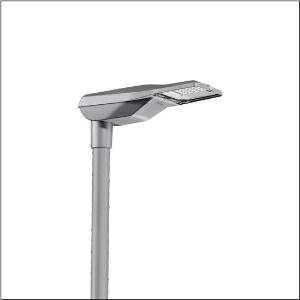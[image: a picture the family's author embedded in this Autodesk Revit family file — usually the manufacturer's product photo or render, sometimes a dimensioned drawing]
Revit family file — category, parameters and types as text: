
# Revit family: streetlight_sl_21_iq_micro___st1_0ab_5xe1m31d08db_7599
name_source: partatom
category: Lighting Fixtures
units: mm (PartAtom-declared; Revit-internal decimal feet)

## family parameters
Cut with Voids When Loaded = No
Host = Face
Light Source = No
Part Type = Normal
Room Calculation Point = No
Round Connector Dimension = Use Diameter
Shared = No

## types (1)
- --- (1 x LED, 4240 lm, 36.4 W, 3000K)
    Apparent Load = 36 VA
    CIE Flux Codes = 38 73 97 100 100
    Color Rendering = 70
    Color Temperature = 3000K
    Default Elevation = 1800 mm
    Description = Streetlight SL 21 iQ micro, mast luminaire, primary light control with lens, of PMMA, primary optical cover: cover, of toughened safety glass, transparent, light distribution: ST1.0aB, light emission: direct distribution, primary light characteristic: asymmetric, installation type: post-top, side-entry, LED, High Power LED, rated luminous flux: 4.240lm, luminous efficacy: 117lm/W, light colour: 730, colour temperature: 3000K, control: Auto-Match, Temp-Guard, Lumen-Switch, Night-Set, Smart-Wire, Light-Fading, Desk-Remote (wireless, voltage-free reading and setting of iQ features in the workshop via application-optimized NFC function/RFID function), optimised constant luminous flux control (CLO 2.0), presetting dimming linear, mains connection: 220..240V, AC, 50/60Hz, start of lifetime: 36W, end of service life: 38W, reduction: 16W, luminaire housing, of diecast aluminium, powder-coated, Siteco® metallic grey (DB 702S), corrosivity category C5 mid according to DIN EN ISO 12944, please order mast flange separately, inclination adjustable: 0°, 5°, 10°, 15°, sealing non-destructively replaceable, multi-level sealing system, length: 528mm, width: 235mm, height: 110mm, mast flange for spigot size: 42mm (side-entry): 5XC10008XM4, 60/48mm (side-entry/post-top): 5XC10108XM2, 76/60mm (side-entry/post-top): 5XC10108XM1, protection rating (complete): IP66, insulation class (complete): insulation class II (safety insulation), certification: CE, ENEC, ENEC+, VDE, impact resistance: IK09, permissible operating ambient temperature for outdoor applications: -40..+50°C, standard-compliant lighting for roads and squares, packaging unit: 1 piece

Light Distribution: ST1.0aB
    Height = 110 mm
    Lamp = 1 x LED
    Lamp Light Flux = 4240 lm
    Lamp Power = 36.4 W
    Lamp count = 1
    Length = 528 mm
    Luminous efficacy = 116 lm/W
    Manufacturer = Siteco
    ModVariant = No
    Model = 5XE1M31D08DB
    Number of Poles = 1
    OnlyDefault = Yes
    Power Factor = 1
    Product Name = Streetlight SL 21 iQ micro | ST1.0aB
    Product group = mast luminaire | pylon top
    ProductGroupID = 6100
    Protection Class = Protection class II
    Protection Degree = IP 66
    RLX_Detail_Level = 1
    RLX_Emergency_Light_Flux = 0 lm
    RLX_Emergency_Type = 0
    RLX_Emergency_Type_DB = No
    RlxData = <blob elided: 98913 chars, md5=5ed4cde0>
    Socket = socket
    Standby Power = 0 W
    System Light Flux = 4240 lm
    System Power = 36 W
    Type Comments = factory setting: luminous flux: 100 % | dim-lin: 254 | 715 mA
    Type Image = l_1006881.jpg
    URL = http://relux.com
    VarID = @adj_086395
    Voltage = 0 V
    Weight = 0.00 kg
    Width = 235 mm

## geometry (parser evidence)
native form markers: Blend x4, Sweep x11
no freeform markers — native parametric forms only
